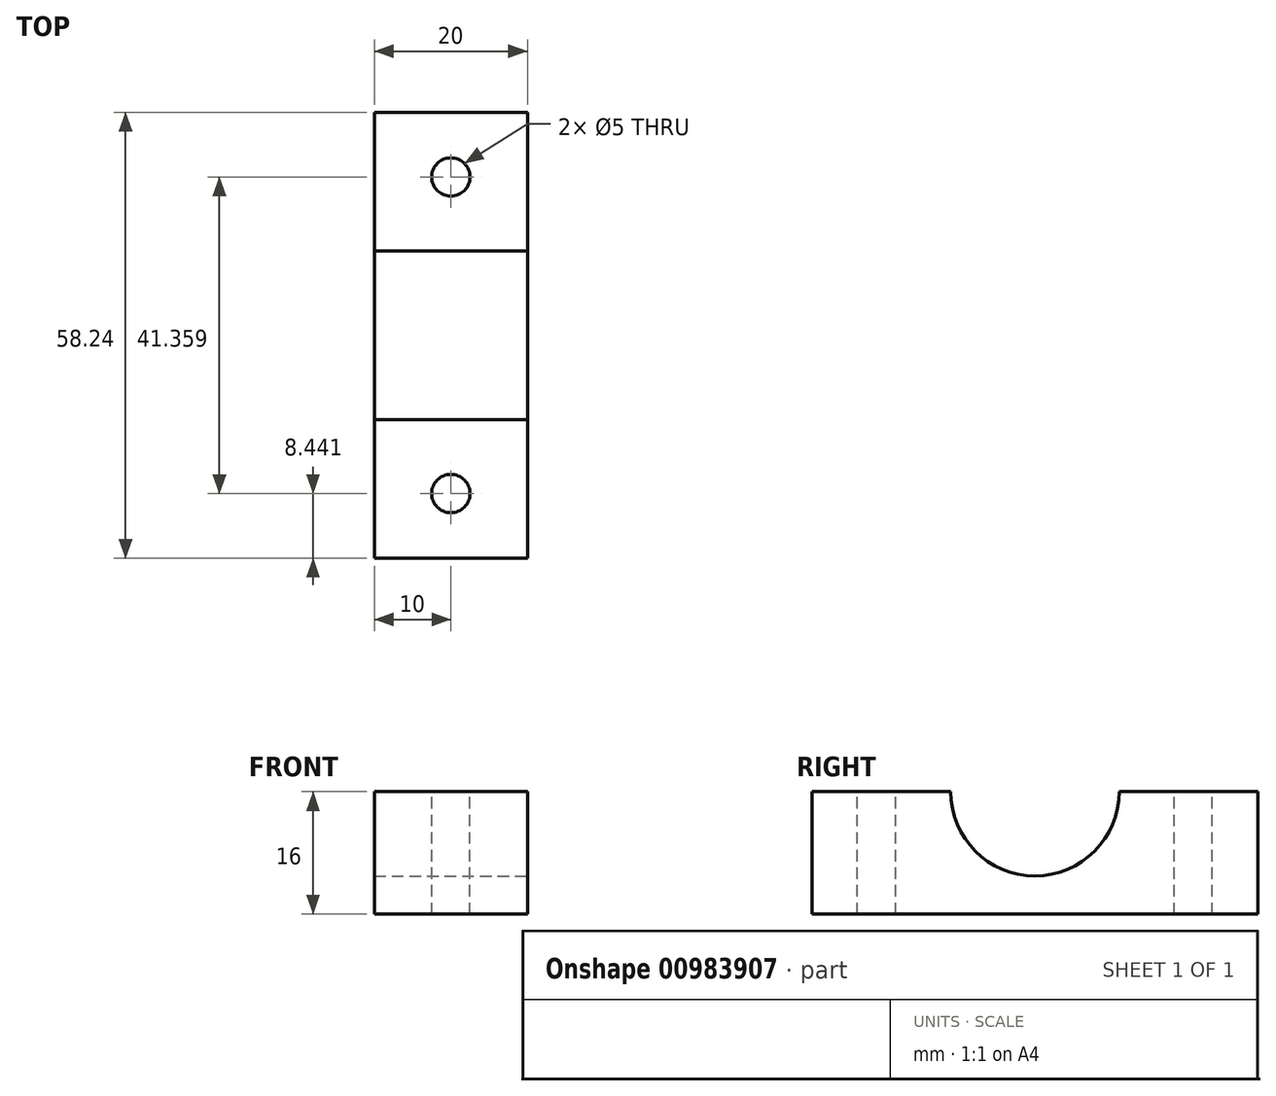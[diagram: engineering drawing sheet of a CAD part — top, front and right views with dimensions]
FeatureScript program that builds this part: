
annotation { "Feature Type Name" : "Feature", "Feature Type Description" : "" }
export const myFeature = defineFeature(function(context is Context, id is Id, definition is map)
    precondition{}
    {
        {
            var Q0;
            Q0=qCreatedBy(makeId("Right.planeOp"),FACE);
            var sketch = newSketch(context, id + "F0", { "sketchPlane" : qUnion([Q0])});
            skArc(sketch, "E0", {"start": v(-11, 0) * mm, "mid": v(-7.78, -7.78) * mm, "end": v(0, -11) * mm});
            skLineSegment(sketch, "E1", {"start": v(-11, 0) * mm, "end": v(-29.12, 0) * mm});
            skLineSegment(sketch, "E2", {"start": v(-29.12, 0) * mm, "end": v(-29.12, -16) * mm});
            skLineSegment(sketch, "E3", {"start": v(0, -11) * mm, "end": v(0, -16) * mm});
            skLineSegment(sketch, "E4", {"start": v(-29.12, -16) * mm, "end": v(0, -16) * mm});
            skSolve(sketch);
        }
        {
            var Q0;
            Q0=makeQuery(id+"F0.imprint","IMPRINT",FACE,{"disambiguationData":[TD([[makeQuery(id+"F0.imprint","IMPRINT",EDGE,{"derivedFrom":sQuery(id+"F0.wireOp",EDGE,"E0")}),-1.0]])]});
            extrude(context, id + "F1", {"entities" : qUnion([Q0]), "oppositeDirection" : true, "depth" : 20 * mm, "offsetDistance" : 25 * mm});
        }
        {
            var Q0;
            Q0=makeQuery(id+"F1.opExtrude","SWEPT_FACE",FACE,{"disambiguationData":[OSD([sQuery(id+"F0.wireOp",EDGE,"E1")])]});
            cPlane(context, id + "F2", {"entities" : qUnion([Q0]), "cplaneType" : CPlaneType.OFFSET, "offset" : 0 * mm, "width" : 150 * mm, "height" : 150 * mm});
        }
        {
            var Q0;
            Q0=qCreatedBy(id+"F2.planeOp",FACE);
            var sketch = newSketch(context, id + "F3", { "sketchPlane" : qUnion([Q0])});
            skLineSegment(sketch, "E5", {"start": v(-10, -29.12) * mm, "end": v(-10, -20.68) * mm});
            skCircle(sketch, "E6", {"center": v(-10, -20.68) * mm, "radius": 2.5 * mm});
            skSolve(sketch);
        }
        {
            var Q0;
            Q0=makeQuery(id+"F3.imprint","IMPRINT",FACE,{"disambiguationData":[TD([[makeQuery(id+"F3.imprint","IMPRINT",EDGE,{"derivedFrom":sQuery(id+"F3.wireOp",EDGE,"E6")}),1.0]])]});
            extrude(context, id + "F4", {"entities" : qUnion([Q0]), "operationType" : NewBodyOperationType.REMOVE, "oppositeDirection" : true, "depth" : 25 * mm, "offsetDistance" : 25 * mm});
        }
        {
            var Q0;
            Q0=makeQuery(id+"F1.opExtrude","SWEPT_BODY",BODY,{"disambiguationData":[OSD([sQuery(id+"F0.wireOp",EDGE,"E0"),sQuery(id+"F0.wireOp",EDGE,"E1"),sQuery(id+"F0.wireOp",EDGE,"E2"),sQuery(id+"F0.wireOp",EDGE,"E3"),sQuery(id+"F0.wireOp",EDGE,"E4")])]});
            var Q1;
            Q1=makeQuery(id+"F1.opExtrude","SWEPT_FACE",FACE,{"disambiguationData":[OSD([sQuery(id+"F0.wireOp",EDGE,"E3")])]});
            mirror(context, id + "F5", {"operationType" : NewBodyOperationType.ADD, "entities" : qUnion([Q0]), "mirrorPlane" : qUnion([Q1])});
        }
    });
